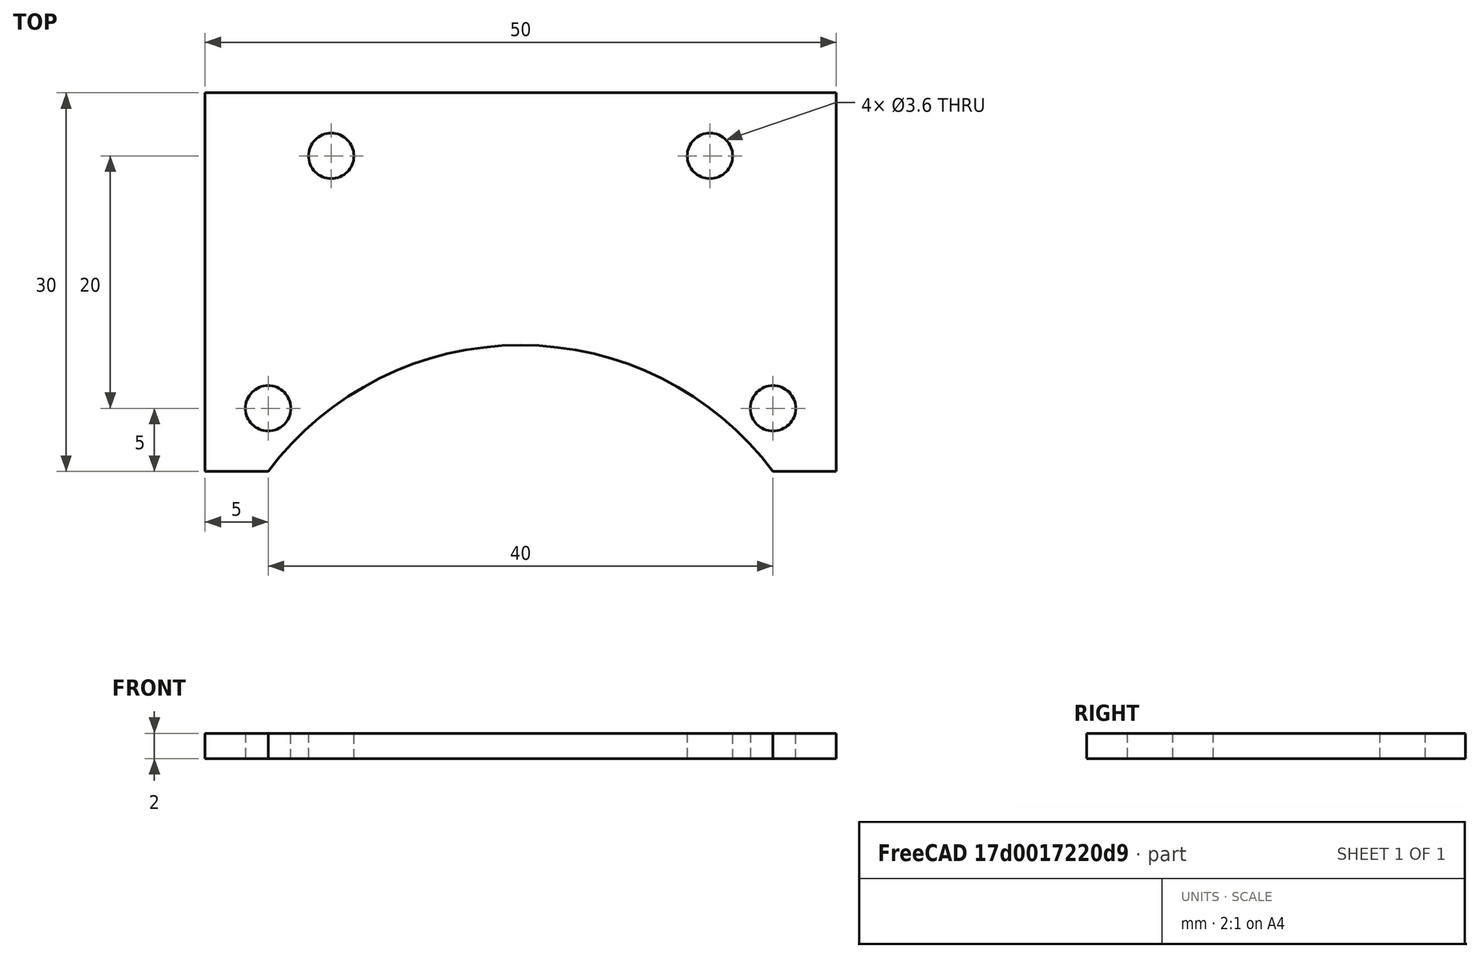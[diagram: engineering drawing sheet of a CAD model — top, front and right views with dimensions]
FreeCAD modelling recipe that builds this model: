
FCSTD DOCUMENT
Label: YCableSupport
objects: Sketcher::SketchObject×1, PartDesign::Pad×1
note: 3 computed .brp shape members not serialized (recipe doc carries the construction recipe); baked Part::Feature solids carry a one-line shape summary decoded from their .brp

FEATURE [Sketcher::SketchObject] Sketch
  sketch-geometry (17):
    g0: LineSegment StartX=5 StartY=0 StartZ=0 EndX=0 EndY=0 EndZ=0
    g1: LineSegment StartX=0 StartY=0 StartZ=0 EndX=0 EndY=30 EndZ=0
    g2: LineSegment StartX=0 StartY=30 StartZ=0 EndX=50 EndY=30 EndZ=0
    g3: LineSegment StartX=50 StartY=30 StartZ=0 EndX=50 EndY=0 EndZ=0
    g4: LineSegment StartX=50 StartY=0 StartZ=0 EndX=45 EndY=0 EndZ=0
    g5: LineSegment [constr] StartX=45 StartY=0 StartZ=0 EndX=5 EndY=0 EndZ=0
    g6: ArcOfCircle CenterX=25 CenterY=-15 CenterZ=0 NormalX=0 NormalY=0 NormalZ=1 Radius=25 StartAngle=0.643501 EndAngle=2.49809
    g7: Circle CenterX=5 CenterY=5 CenterZ=0 NormalX=0 NormalY=0 NormalZ=1 Radius=1.8
    g8: Circle CenterX=45 CenterY=5 CenterZ=0 NormalX=0 NormalY=0 NormalZ=1 Radius=1.8
    g9: LineSegment [constr] StartX=5 StartY=5 StartZ=0 EndX=45 EndY=5 EndZ=0
    g10: LineSegment [constr] StartX=45 StartY=5 StartZ=0 EndX=45 EndY=-15 EndZ=0
    g11: LineSegment [constr] StartX=45 StartY=-15 StartZ=0 EndX=25 EndY=-15 EndZ=0
    g12: LineSegment [constr] StartX=25 StartY=-15 StartZ=0 EndX=5 EndY=-15 EndZ=0
    g13: LineSegment [constr] StartX=5 StartY=-15 StartZ=0 EndX=5 EndY=5 EndZ=0
    g14: LineSegment [constr] StartX=10 StartY=25 StartZ=0 EndX=40 EndY=25 EndZ=0
    g15: Circle CenterX=40 CenterY=25 CenterZ=0 NormalX=0 NormalY=0 NormalZ=1 Radius=1.8
    g16: Circle CenterX=10 CenterY=25 CenterZ=0 NormalX=0 NormalY=0 NormalZ=1 Radius=1.8
  constraints (47):
    c: Horizontal(g0)
    c: Coincident(g0,g1)
    c: Vertical(g1)
    c: Coincident(g1,g2)
    c: Horizontal(g2)
    c: Coincident(g2,g3)
    c: Vertical(g3)
    c: Coincident(g3,g4)
    c: Horizontal(g4)
    c: Coincident(g4,g5)
    c: Horizontal(g5)
    c: Coincident(g5,g0)
    c: Coincident(g6,g0)
    c: Coincident(g6,g4)
    c: Coincident(g9,g7)
    c: Coincident(g9,g8)
    c: Horizontal(g9)
    c: Equal(g8,g7)
    c: Radius(g7) = 1.8
    c: DistanceX(g7,g0) = -5
    c: DistanceX(g8,g3) = 5
    c: DistanceX(g2) = 50
    c: DistanceX(g0) = -5
    c: DistanceY(g7,g0) = -5
    c: Coincident(g10,g8)
    c: Vertical(g10)
    c: Coincident(g10,g11)
    c: Horizontal(g11)
    c: Coincident(g11,g12)
    c: Horizontal(g12)
    c: Coincident(g12,g13)
    c: Coincident(g13,g7)
    c: Vertical(g13)
    c: Coincident(g6,g11)
    c: Equal(g11,g12)
    c: DistanceY(g13) = 20
    c: DistanceY(g3) = -30
    c: DistanceX(g0) = 0
    c: DistanceY(g0) = 0
    c: Horizontal(g14)
    c: Coincident(g15,g14)
    c: Coincident(g16,g14)
    c: Equal(g16,g7)
    c: Equal(g15,g7)
    c: DistanceX(g14,g1) = -10
    c: DistanceX(g14,g2) = 10
    c: DistanceY(g14,g1) = 5
FEATURE [PartDesign::Pad] Pad
  Length = 2
  MirroredExtent = false
  Sketch = -> Sketch
